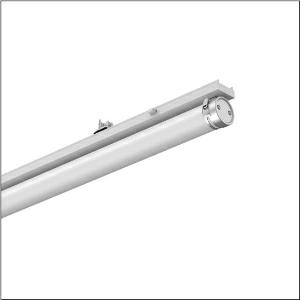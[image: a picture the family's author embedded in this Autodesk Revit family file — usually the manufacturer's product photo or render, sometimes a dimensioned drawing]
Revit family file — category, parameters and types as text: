
# Revit family: monsun_r__31_tube_51ft10mn4a0atr2_ffb0
name_source: partatom
category: Lighting Fixtures
units: mm (PartAtom-declared; Revit-internal decimal feet)

## family parameters
Cut with Voids When Loaded = No
Host = Face
Light Source = No
Part Type = Normal
Room Calculation Point = No
Round Connector Dimension = Use Diameter
Shared = No

## types (1)
- --- (1 x LED, 10000 lm, 58 W, 4000K)
    Apparent Load = 58 VA
    CIE Flux Codes = 42 71 90 91 100
    Color Rendering = 80
    Color Temperature = 4000K
    Default Elevation = 1800 mm
    Description = Monsun® 31 Tube, tubular luminaire, primary optical cover: diffuser, of PMMA, light emission: direct distribution, primary light characteristic: symmetric, LED, rated luminous flux: 10.000lm, luminous efficacy: 172lm/W, light colour: 840, colour temperature: 4000K, with with 1 terminal, 3-pole, max. 2.5mm², mains connection: 220..240V, AC, 50/60Hz, rated input power: 58W, housing, cylindrical, of PMMA, semi-transparent, matt white, with luminaire and ceiling fastening, V4A, mounting with brackets of stainless steel, length: 1.500mm, diameter: 75mm, end cap, of stainless steel (V4A), protection rating (complete): IP20, protection rating (lamp compartment): IP67/69K, insulation class (complete): insulation class I (protective earthing), certification: CE, UKCA, impact resistance: IK06, permissible operating ambient temperature: -20..+40°C, corresponds to IFS (International Featured Standards) requirements for safety and quality in the food industry, contact your sales advisor before using the luminaires in applications with unclear chemical exposure, large temperature fluctuations or condensation-forming humidity, packaging unit: 1 piece
    Height = 132 mm
    Lamp = 1 x LED
    Lamp Light Flux = 10000 lm
    Lamp Power = 58 W
    Lamp count = 1
    Length = 1500 mm
    Luminous efficacy = 172 lm/W
    Manufacturer = Siteco
    ModVariant = No
    Model = 51FT10MN4A0ATR2
    Mounting Place = Ceiling
    Mounting Type = Pendant
    Number of Poles = 1
    OnlyDefault = Yes
    Power Factor = 1
    Product Name = Monsun® 31 Tube
    Product group = tubular luminaire
    ProductGroupID = 906
    Protection Class = Protection class I
    Protection Degree = IP 20
    RLX_Detail_Level = 1
    RLX_Emergency_Light_Flux = 0 lm
    RLX_Emergency_Type = 0
    RLX_Emergency_Type_DB = No
    RlxData = <blob elided: 32277 chars, md5=dabdbd56>
    Socket = socket
    Standby Power = 0 W
    System Light Flux = 10000 lm
    System Power = 58 W
    Type Comments = factory setting: luminous flux: 100 % | (OFF | OFF | OFF | OFF) | 350 mA
    Type Image = l_1242814.jpg
    URL = http://relux.com
    VarID = @adj_092731
    Voltage = 0 V
    Weight = 0.00 kg
    Width = 79 mm

## geometry (parser evidence)
native form markers: Blend x4, Sweep x10
no freeform markers — native parametric forms only
